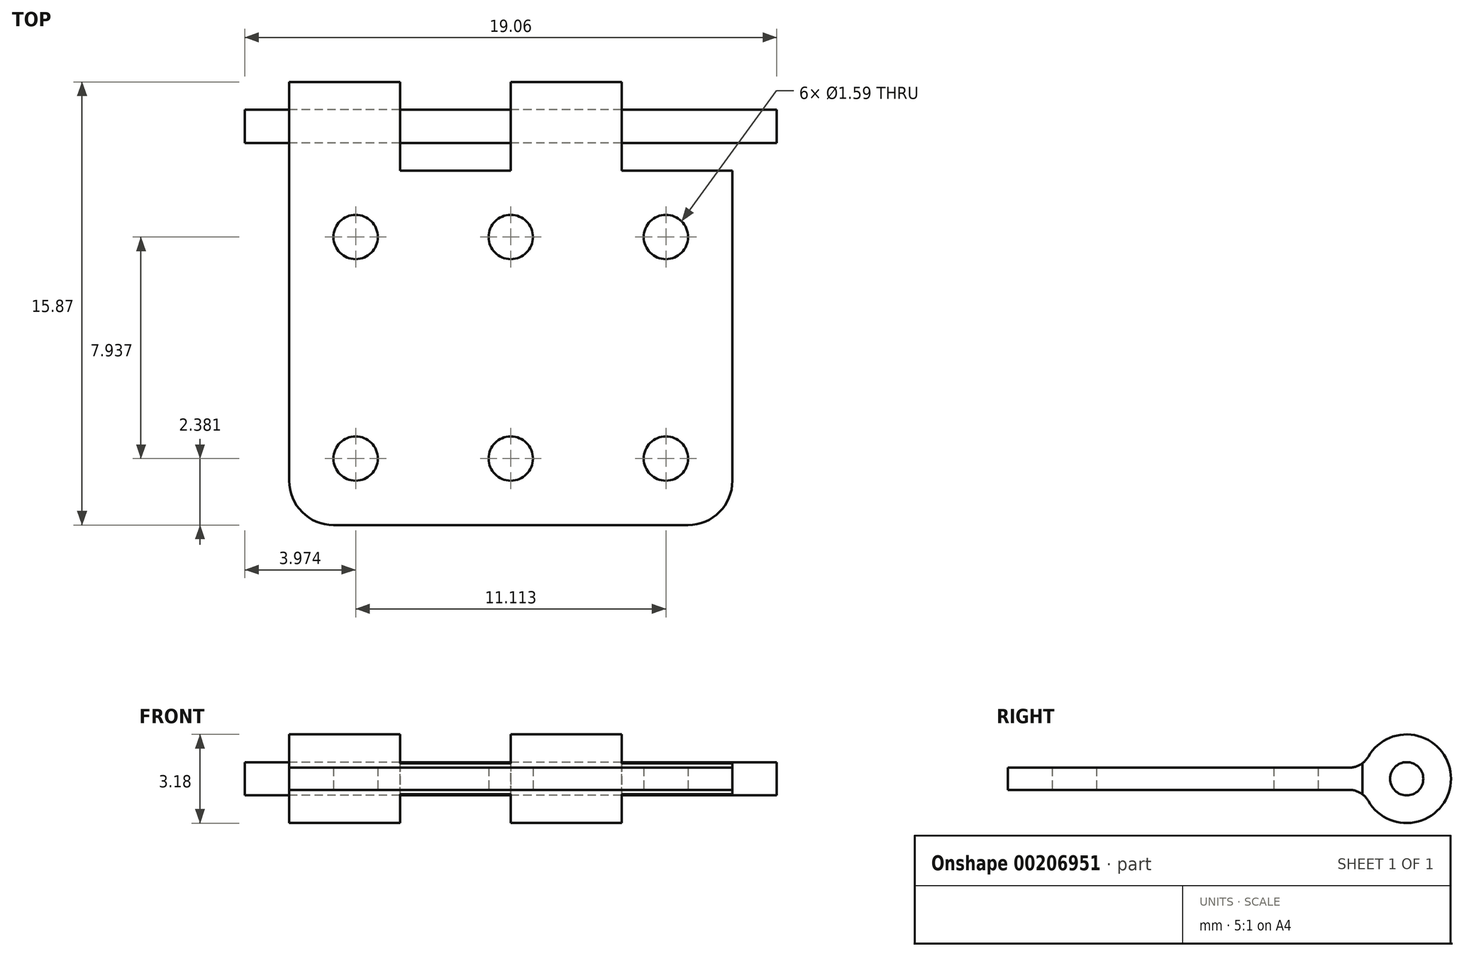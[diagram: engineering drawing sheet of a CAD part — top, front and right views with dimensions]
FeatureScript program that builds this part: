
annotation { "Feature Type Name" : "Feature", "Feature Type Description" : "" }
export const myFeature = defineFeature(function(context is Context, id is Id, definition is map)
    precondition{}
    {
        {
            var Q0;
            Q0=qCreatedBy(makeId("Top.planeOp"),FACE);
            var sketch = newSketch(context, id + "F0", { "sketchPlane" : qUnion([Q0])});
            skLineSegment(sketch, "E0.bottom", {"start": v(-7.94, 3.18) * mm, "end": v(-3.97, 3.18) * mm});
            skLineSegment(sketch, "E0.top", {"start": v(-6.35, -12.7) * mm, "end": v(6.35, -12.7) * mm});
            skLineSegment(sketch, "E0.left", {"start": v(-7.94, 3.18) * mm, "end": v(-7.94, -11.11) * mm});
            skLineSegment(sketch, "E1", {"start": v(0, 0) * mm, "end": v(0, -12.7) * mm, "construction": true});
            skPoint(sketch, "E2.visualSharp", {"position": v(-7.94, -12.7) * mm});
            skArc(sketch, "E2.filletArc", {"start": v(-7.94, -11.11) * mm, "mid": v(-7.47, -12.24) * mm, "end": v(-6.35, -12.7) * mm});
            skLineSegment(sketch, "E3", {"start": v(-7.94, -10.32) * mm, "end": v(7.94, -10.32) * mm, "construction": true});
            skLineSegment(sketch, "E4", {"start": v(-7.94, -2.38) * mm, "end": v(7.94, -2.38) * mm, "construction": true});
            skLineSegment(sketch, "E5", {"start": v(-5.56, 3.18) * mm, "end": v(-5.56, -12.7) * mm, "construction": true});
            skLineSegment(sketch, "E6", {"start": v(5.56, 0) * mm, "end": v(5.56, -12.7) * mm, "construction": true});
            skLineSegment(sketch, "E7", {"start": v(-3.97, 3.18) * mm, "end": v(-3.97, 0) * mm});
            skLineSegment(sketch, "E8", {"start": v(3.97, 3.18) * mm, "end": v(3.97, 0) * mm});
            skLineSegment(sketch, "E9", {"start": v(-3.97, 0) * mm, "end": v(0, 0) * mm});
            skLineSegment(sketch, "E10", {"start": v(3.97, 0) * mm, "end": v(7.94, 0) * mm});
            skLineSegment(sketch, "E11", {"start": v(0, 3.18) * mm, "end": v(3.97, 3.18) * mm});
            skLineSegment(sketch, "E12", {"start": v(7.94, 0) * mm, "end": v(7.94, -11.11) * mm});
            skPoint(sketch, "E13.visualSharp", {"position": v(7.94, -12.7) * mm});
            skArc(sketch, "E13.filletArc", {"start": v(6.35, -12.7) * mm, "mid": v(7.47, -12.24) * mm, "end": v(7.94, -11.11) * mm});
            skCircle(sketch, "E14", {"center": v(-5.56, -2.38) * mm, "radius": 0.8 * mm});
            skCircle(sketch, "E15", {"center": v(0, -2.38) * mm, "radius": 0.8 * mm});
            skCircle(sketch, "E16", {"center": v(5.56, -2.38) * mm, "radius": 0.8 * mm});
            skCircle(sketch, "E17", {"center": v(-5.56, -10.32) * mm, "radius": 0.8 * mm});
            skCircle(sketch, "E18", {"center": v(0, -10.32) * mm, "radius": 0.8 * mm});
            skCircle(sketch, "E19", {"center": v(5.56, -10.32) * mm, "radius": 0.8 * mm});
            skLineSegment(sketch, "E20", {"start": v(0, 0) * mm, "end": v(0, 3.18) * mm});
            skSolve(sketch);
        }
        {
            var Q0;
            Q0=qCreatedBy(makeId("Right.planeOp"),FACE);
            var sketch = newSketch(context, id + "F1", { "sketchPlane" : qUnion([Q0])});
            skLineSegment(sketch, "E21", {"start": v(-12.7, -0.4) * mm, "end": v(-0.47, -0.4) * mm});
            skLineSegment(sketch, "E22", {"start": v(-0.47, 0.4) * mm, "end": v(-12.7, 0.4) * mm});
            skLineSegment(sketch, "E23", {"start": v(-12.7, 0.4) * mm, "end": v(-12.7, -0.4) * mm});
            skCircle(sketch, "E24", {"center": v(1.59, 0) * mm, "radius": 0.6 * mm});
            skArc(sketch, "E25", {"start": v(0.21, -0.8) * mm, "mid": v(3.18, 0) * mm, "end": v(0.21, 0.8) * mm});
            skPoint(sketch, "E26.visualSharp", {"position": v(0.05, 0.4) * mm});
            skArc(sketch, "E26.filletArc", {"start": v(-0.47, 0.4) * mm, "mid": v(-0.08, 0.5) * mm, "end": v(0.21, 0.8) * mm});
            skPoint(sketch, "E27.visualSharp", {"position": v(0.05, -0.4) * mm});
            skArc(sketch, "E27.filletArc", {"start": v(0.21, -0.8) * mm, "mid": v(-0.08, -0.5) * mm, "end": v(-0.47, -0.4) * mm});
            skSolve(sketch);
        }
        {
            var Q0;
            Q0=makeQuery(id+"F0.imprint","IMPRINT",FACE,{"disambiguationData":[TD([[makeQuery(id+"F0.imprint","IMPRINT",EDGE,{"derivedFrom":sQuery(id+"F0.wireOp",EDGE,"E0.bottom")}),-1.0]])]});
            extrude(context, id + "F2", {"entities" : qUnion([Q0]), "endBound" : BoundingType.SYMMETRIC, "depth" : 3.17 * mm});
        }
        {
            var Q0;
            Q0=makeQuery(id+"F1.imprint","IMPRINT",FACE,{"disambiguationData":[TD([[makeQuery(id+"F1.imprint","IMPRINT",EDGE,{"derivedFrom":sQuery(id+"F1.wireOp",EDGE,"E21")}),1.0]])]});
            extrude(context, id + "F3", {"entities" : qUnion([Q0]), "operationType" : NewBodyOperationType.INTERSECT, "endBound" : BoundingType.SYMMETRIC, "depth" : 25.4 * mm});
        }
        {
            var Q0;
            Q0=makeQuery(id+"F1.imprint","IMPRINT",FACE,{"disambiguationData":[TD([[makeQuery(id+"F1.imprint","IMPRINT",EDGE,{"derivedFrom":sQuery(id+"F1.wireOp",EDGE,"E24")}),1.0]])]});
            extrude(context, id + "F4", {"entities" : qUnion([Q0]), "endBound" : BoundingType.SYMMETRIC, "depth" : 19.05 * mm});
        }
    });
